# Revit family: MP 550 Ultra (a)
name_source: partatom
category: Equipement spécialisé
revit_build: Autodesk Revit LT 2015 (Build: 20140606_1530(x64)
units: mm (PartAtom-declared; Revit-internal decimal feet)

## types (3) — shared parameters
Apparent Power = 0 VA
Depth = 125 mm  [stored 0.410105 ft]
Depth Electrique connexion = 63 mm  [stored 0.206693 ft]
Description = MIXERS PLONGEANTS GAMME LARGE
Fabricant = ROBOT COUPE
Height = 940 mm  [stored 3.08399 ft]
Height Electrique connexion = 930 mm  [stored 3.05118 ft]
Modèle = MP 550 Ultra
Phase = 1
Speeds (Rpm) = 9000
URL = www.robot-coupe.com
Watts = 750 W
Weight = 6.6 kg
Width = 173 mm  [stored 0.567585 ft]
water = Connector
zero-valued in all types: Cold water supply, Cold water supply height, Used water, Waste water height

## per-type parameters (varying)
| type | Amps | Cycle | Volts |
| MP 550 Ultra   230/50/1 | 3.5 A | 50 Hz | 230 V |
| MP 550 Ultra   120/60/1 | 6.5 A | 60 Hz | 120 V |
| MP 550 Ultra   240/50/1 | 2.1 A | 50 Hz | 240 V |

note: [stored X ft] marks values corroborated as IEEE doubles in the binary element streams (Revit-internal decimal feet)

## geometry (parser evidence)
native form markers: Blend x106, Sweep x10
no freeform markers — native parametric forms only
